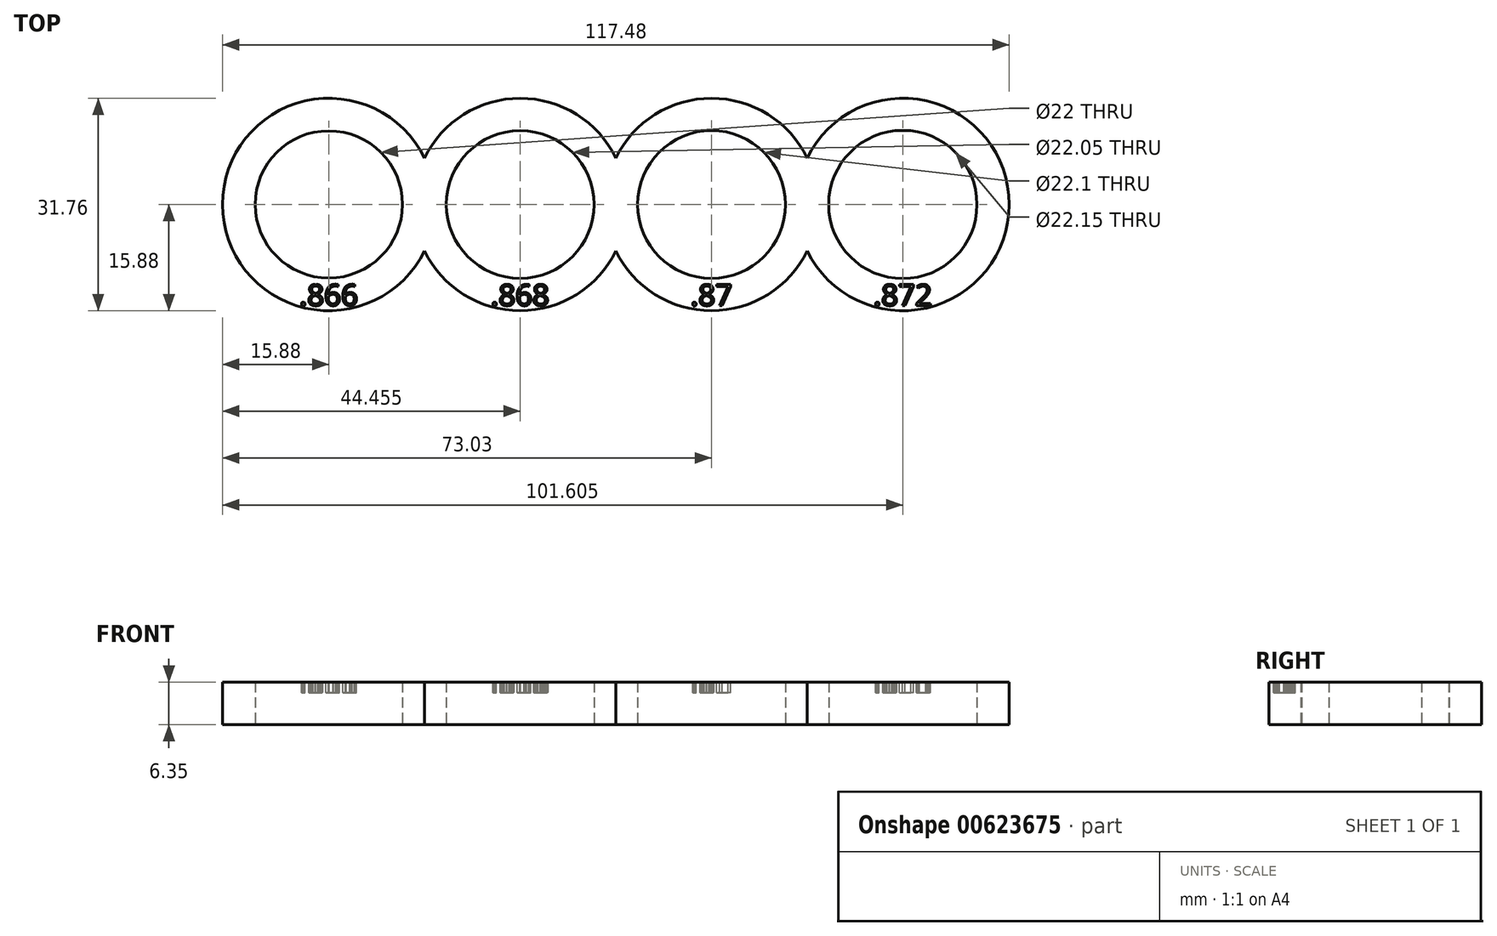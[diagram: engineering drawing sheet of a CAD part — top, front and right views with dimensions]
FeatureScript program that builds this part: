
annotation { "Feature Type Name" : "Feature", "Feature Type Description" : "" }
export const myFeature = defineFeature(function(context is Context, id is Id, definition is map)
    precondition{}
    {
        {
            var Q0;
            Q0=qCreatedBy(makeId("Top.planeOp"),FACE);
            var sketch = newSketch(context, id + "F0", { "sketchPlane" : qUnion([Q0])});
            skCircle(sketch, "E0", {"center": v(0, 0) * mm, "radius": 11 * mm});
            skCircle(sketch, "E1", {"center": v(28.58, 0) * mm, "radius": 11.02 * mm});
            skCircle(sketch, "E2", {"center": v(57.15, 0) * mm, "radius": 11.05 * mm});
            skCircle(sketch, "E3", {"center": v(85.73, 0) * mm, "radius": 11.07 * mm});
            skArc(sketch, "E4", {"start": v(14.29, 6.92) * mm, "mid": v(-15.88, 0) * mm, "end": v(14.29, -6.92) * mm});
            skArc(sketch, "E5", {"start": v(14.29, -6.92) * mm, "mid": v(28.58, -15.88) * mm, "end": v(42.86, -6.92) * mm});
            skArc(sketch, "E6", {"start": v(42.86, -6.92) * mm, "mid": v(57.15, -15.88) * mm, "end": v(71.44, -6.92) * mm});
            skArc(sketch, "E7", {"start": v(71.44, -6.92) * mm, "mid": v(101.6, 0) * mm, "end": v(71.44, 6.92) * mm});
            skArc(sketch, "E8.trimOffspring", {"start": v(42.86, 6.92) * mm, "mid": v(28.57, 15.88) * mm, "end": v(14.29, 6.92) * mm});
            skArc(sketch, "E9.trimOffspring", {"start": v(71.44, 6.92) * mm, "mid": v(57.15, 15.88) * mm, "end": v(42.86, 6.92) * mm});
            skSolve(sketch);
        }
        {
            var Q0;
            Q0=makeQuery(id+"F0.imprint","IMPRINT",FACE,{"disambiguationData":[TD([[makeQuery(id+"F0.imprint","IMPRINT",EDGE,{"derivedFrom":sQuery(id+"F0.wireOp",EDGE,"E0")}),-1.0]])]});
            extrude(context, id + "F1", {"entities" : qUnion([Q0]), "depth" : 6.35 * mm, "offsetDistance" : 25.4 * mm});
        }
        {
            var Q0;
            Q0=makeQuery(id+"F1.opExtrude","CAP_FACE",FACE,{"disambiguationData":[OSD([sQuery(id+"F0.wireOp",EDGE,"E0"),sQuery(id+"F0.wireOp",EDGE,"E1"),sQuery(id+"F0.wireOp",EDGE,"E2"),sQuery(id+"F0.wireOp",EDGE,"E3"),sQuery(id+"F0.wireOp",EDGE,"E4"),sQuery(id+"F0.wireOp",EDGE,"E5"),sQuery(id+"F0.wireOp",EDGE,"E6"),sQuery(id+"F0.wireOp",EDGE,"E7"),sQuery(id+"F0.wireOp",EDGE,"E8.trimOffspring"),sQuery(id+"F0.wireOp",EDGE,"E9.trimOffspring")])],"isStart":false});
            var sketch = newSketch(context, id + "F2", { "sketchPlane" : qUnion([Q0])});
            skText(sketch, "E10", { "text": ".866", "fontName": "OpenSans-Regular.ttf"});
            skText(sketch, "E11", { "text": ".868", "fontName": "OpenSans-Regular.ttf"});
            skText(sketch, "E12", { "text": ".87", "fontName": "OpenSans-Regular.ttf"});
            skText(sketch, "E13", { "text": ".872", "fontName": "OpenSans-Regular.ttf"});
            skCircle(sketch, "E14.0", {"center": v(28.58, 0) * mm, "radius": 11.02 * mm});
            skCircle(sketch, "E15.0", {"center": v(57.15, 0) * mm, "radius": 11.05 * mm});
            skCircle(sketch, "E16.0", {"center": v(85.73, 0) * mm, "radius": 11.07 * mm});
            const initialGuessF2  = {"E10": [-0.0044, -0.01511, 1, 0, 0.00318], "E11": [0.02418, -0.01511, 1, 0, 0.00317], "E12": [0.05401, -0.01511, 1, 0, 0.00318], "E13": [0.08133, -0.01511, 1, 0, 0.00318]};
            skSetInitialGuess(sketch, initialGuessF2);
            skSolve(sketch);
        }
        {
            var Q0;
            Q0=makeQuery(id+"F2.imprint","IMPRINT",FACE,{"disambiguationData":[TD([[makeQuery(id+"F2.imprint","IMPRINT",EDGE,{"derivedFrom":sQuery(id+"F2.wireOp",EDGE,"E10.sketch_text.stroke-8")}),-1.0]])]});
            var Q1;
            Q1=makeQuery(id+"F2.imprint","IMPRINT",FACE,{"disambiguationData":[TD([[makeQuery(id+"F2.imprint","IMPRINT",EDGE,{"derivedFrom":sQuery(id+"F2.wireOp",EDGE,"E10.sketch_text.stroke-39")}),-1.0]])]});
            var Q2;
            Q2=makeQuery(id+"F2.imprint","IMPRINT",FACE,{"disambiguationData":[TD([[makeQuery(id+"F2.imprint","IMPRINT",EDGE,{"derivedFrom":sQuery(id+"F2.wireOp",EDGE,"E10.sketch_text.stroke-64")}),-1.0]])]});
            var Q3;
            Q3=makeQuery(id+"F2.imprint","IMPRINT",FACE,{"disambiguationData":[TD([[makeQuery(id+"F2.imprint","IMPRINT",EDGE,{"derivedFrom":sQuery(id+"F2.wireOp",EDGE,"E10.sketch_text.stroke-0")}),-1.0]])]});
            var Q4;
            Q4=makeQuery(id+"F2.imprint","IMPRINT",FACE,{"disambiguationData":[TD([[makeQuery(id+"F2.imprint","IMPRINT",EDGE,{"derivedFrom":sQuery(id+"F2.wireOp",EDGE,"E11.sketch_text.stroke-8")}),-1.0]])]});
            var Q5;
            Q5=makeQuery(id+"F2.imprint","IMPRINT",FACE,{"disambiguationData":[TD([[makeQuery(id+"F2.imprint","IMPRINT",EDGE,{"derivedFrom":sQuery(id+"F2.wireOp",EDGE,"E11.sketch_text.stroke-39")}),-1.0]])]});
            var Q6;
            Q6=makeQuery(id+"F2.imprint","IMPRINT",FACE,{"disambiguationData":[TD([[makeQuery(id+"F2.imprint","IMPRINT",EDGE,{"derivedFrom":sQuery(id+"F2.wireOp",EDGE,"E11.sketch_text.stroke-64")}),-1.0]])]});
            var Q7;
            Q7=makeQuery(id+"F2.imprint","IMPRINT",FACE,{"disambiguationData":[TD([[makeQuery(id+"F2.imprint","IMPRINT",EDGE,{"derivedFrom":sQuery(id+"F2.wireOp",EDGE,"E11.sketch_text.stroke-0")}),-1.0]])]});
            var Q8;
            Q8=makeQuery(id+"F2.imprint","IMPRINT",FACE,{"disambiguationData":[TD([[makeQuery(id+"F2.imprint","IMPRINT",EDGE,{"derivedFrom":sQuery(id+"F2.wireOp",EDGE,"E12.sketch_text.stroke-39")}),-1.0]])]});
            var Q9;
            Q9=makeQuery(id+"F2.imprint","IMPRINT",FACE,{"disambiguationData":[TD([[makeQuery(id+"F2.imprint","IMPRINT",EDGE,{"derivedFrom":sQuery(id+"F2.wireOp",EDGE,"E12.sketch_text.stroke-8")}),-1.0]])]});
            var Q10;
            Q10=makeQuery(id+"F2.imprint","IMPRINT",FACE,{"disambiguationData":[TD([[makeQuery(id+"F2.imprint","IMPRINT",EDGE,{"derivedFrom":sQuery(id+"F2.wireOp",EDGE,"E12.sketch_text.stroke-0")}),-1.0]])]});
            var Q11;
            Q11=makeQuery(id+"F2.imprint","IMPRINT",FACE,{"disambiguationData":[TD([[makeQuery(id+"F2.imprint","IMPRINT",EDGE,{"derivedFrom":sQuery(id+"F2.wireOp",EDGE,"E13.sketch_text.stroke-8")}),-1.0]])]});
            var Q12;
            Q12=makeQuery(id+"F2.imprint","IMPRINT",FACE,{"disambiguationData":[TD([[makeQuery(id+"F2.imprint","IMPRINT",EDGE,{"derivedFrom":sQuery(id+"F2.wireOp",EDGE,"E13.sketch_text.stroke-39")}),-1.0]])]});
            var Q13;
            Q13=makeQuery(id+"F2.imprint","IMPRINT",FACE,{"disambiguationData":[TD([[makeQuery(id+"F2.imprint","IMPRINT",EDGE,{"derivedFrom":sQuery(id+"F2.wireOp",EDGE,"E13.sketch_text.stroke-46")}),-1.0]])]});
            var Q14;
            Q14=makeQuery(id+"F2.imprint","IMPRINT",FACE,{"disambiguationData":[TD([[makeQuery(id+"F2.imprint","IMPRINT",EDGE,{"derivedFrom":sQuery(id+"F2.wireOp",EDGE,"E13.sketch_text.stroke-0")}),-1.0]])]});
            extrude(context, id + "F3", {"entities" : qUnion([Q0, Q1, Q2, Q3, Q4, Q5, Q6, Q7, Q8, Q9, Q10, Q11, Q12, Q13, Q14]), "operationType" : NewBodyOperationType.REMOVE, "oppositeDirection" : true, "depth" : 1.59 * mm, "offsetDistance" : 25.4 * mm});
        }
    });
